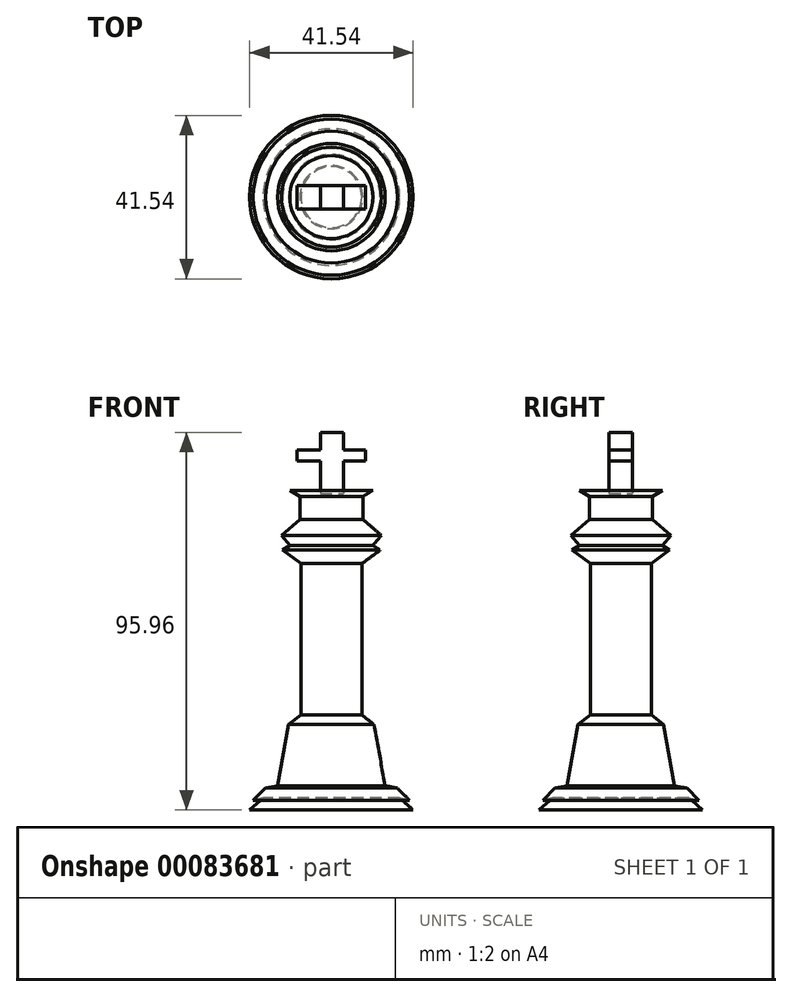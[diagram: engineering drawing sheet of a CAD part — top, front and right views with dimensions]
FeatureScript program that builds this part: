
annotation { "Feature Type Name" : "Feature", "Feature Type Description" : "" }
export const myFeature = defineFeature(function(context is Context, id is Id, definition is map)
    precondition{}
    {
        {
            var Q0;
            Q0=qCreatedBy(makeId("Front.planeOp"),FACE);
            var sketch = newSketch(context, id + "F0", { "sketchPlane" : qUnion([Q0])});
            skLineSegment(sketch, "E0", {"start": v(0, -44.96) * mm, "end": v(20.77, -44.96) * mm});
            skLineSegment(sketch, "E1", {"start": v(20.77, -44.96) * mm, "end": v(17.36, -41.86) * mm});
            skLineSegment(sketch, "E2", {"start": v(17.36, -41.86) * mm, "end": v(19.84, -42.48) * mm});
            skLineSegment(sketch, "E3", {"start": v(19.84, -42.48) * mm, "end": v(16.74, -39.38) * mm});
            skLineSegment(sketch, "E4", {"start": v(16.74, -39.38) * mm, "end": v(13.64, -38.75) * mm});
            skLineSegment(sketch, "E5", {"start": v(13.64, -38.75) * mm, "end": v(10.85, -23.25) * mm});
            skLineSegment(sketch, "E6", {"start": v(10.85, -23.25) * mm, "end": v(7.75, -20.77) * mm});
            skLineSegment(sketch, "E7", {"start": v(7.75, -20.77) * mm, "end": v(7.75, 17.67) * mm});
            skLineSegment(sketch, "E8", {"start": v(7.75, 17.67) * mm, "end": v(12.4, 21.08) * mm});
            skLineSegment(sketch, "E9", {"start": v(12.4, 21.08) * mm, "end": v(10.54, 22.32) * mm});
            skLineSegment(sketch, "E10", {"start": v(10.54, 22.32) * mm, "end": v(12.71, 24.8) * mm});
            skLineSegment(sketch, "E11", {"start": v(12.71, 24.8) * mm, "end": v(8.01, 28.91) * mm});
            skLineSegment(sketch, "E12", {"start": v(8.01, 28.91) * mm, "end": v(8.01, 34.72) * mm});
            skLineSegment(sketch, "E13", {"start": v(8.01, 34.72) * mm, "end": v(10.54, 36.27) * mm});
            skLineSegment(sketch, "E14", {"start": v(10.54, 36.27) * mm, "end": v(0, 36.27) * mm});
            skLineSegment(sketch, "E15", {"start": v(0, 36.27) * mm, "end": v(0, -44.96) * mm});
            skSolve(sketch);
        }
        {
            var Q0;
            Q0=makeQuery(id+"F0.imprint","IMPRINT",FACE,{"disambiguationData":[TD([[makeQuery(id+"F0.imprint","IMPRINT",EDGE,{"derivedFrom":sQuery(id+"F0.wireOp",EDGE,"E0")}),1.0]])]});
            var Q1;
            Q1=sQuery(id+"F0.wireOp",EDGE,"E15");
            revolve(context, id + "F1", {"entities" : qUnion([Q0]), "axis" : qUnion([Q1]), "revolveType" : RevolveType.FULL});
        }
        {
            var Q0;
            Q0=qCreatedBy(makeId("Front.planeOp"),FACE);
            var sketch = newSketch(context, id + "F2", { "sketchPlane" : qUnion([Q0])});
            skLineSegment(sketch, "E16.bottom", {"start": v(-2.8, 51) * mm, "end": v(3.1, 51) * mm});
            skLineSegment(sketch, "E16.top", {"start": v(-2.8, 35.49) * mm, "end": v(3.1, 35.49) * mm});
            skLineSegment(sketch, "E16.left", {"start": v(-2.8, 51) * mm, "end": v(-2.8, 35.49) * mm});
            skLineSegment(sketch, "E16.right", {"start": v(3.1, 51) * mm, "end": v(3.1, 35.49) * mm});
            skLineSegment(sketch, "E17.bottom", {"start": v(-8.68, 46.5) * mm, "end": v(8.68, 46.5) * mm});
            skLineSegment(sketch, "E17.top", {"start": v(-8.68, 43.72) * mm, "end": v(8.68, 43.72) * mm});
            skLineSegment(sketch, "E17.left", {"start": v(-8.68, 46.5) * mm, "end": v(-8.68, 43.72) * mm});
            skLineSegment(sketch, "E17.right", {"start": v(8.68, 46.5) * mm, "end": v(8.68, 43.72) * mm});
            skSolve(sketch);
        }
        {
            var Q0;
            {var subQ0=sQuery(id+"F2.wireOp",EDGE,"E16.top");Q0=makeQuery(id+"F2.imprint","IMPRINT",FACE,{"disambiguationData":[TD([[makeQuery(id+"F2.imprint","IMPRINT",EDGE,{"derivedFrom":subQ0}),1.0]])]});}
            var Q1;
            {var subQ5=sQuery(id+"F2.wireOp",EDGE,"E17.left");Q1=makeQuery(id+"F2.imprint","IMPRINT",FACE,{"disambiguationData":[TD([[makeQuery(id+"F2.imprint","IMPRINT",EDGE,{"derivedFrom":subQ5}),1.0]])]});}
            var Q2;
            {var subQ0=sQuery(id+"F2.wireOp",EDGE,"E17.bottom");var subQ1=sQuery(id+"F2.wireOp",EDGE,"E16.left");var subQ2=makeQuery(id+"F2.imprint","INTERSECT",VERTEX,{"derivedFrom":[subQ1,subQ0]});Q2=makeQuery(id+"F2.imprint","IMPRINT",FACE,{"disambiguationData":[TD([[makeQuery(id+"F2.imprint","IMPRINT",EDGE,{"disambiguationData":[TD([[subQ2,-1.0]])],"derivedFrom":subQ1}),1.0]])]});}
            var Q3;
            {var subQ5=sQuery(id+"F2.wireOp",EDGE,"E17.right");Q3=makeQuery(id+"F2.imprint","IMPRINT",FACE,{"disambiguationData":[TD([[makeQuery(id+"F2.imprint","IMPRINT",EDGE,{"derivedFrom":subQ5}),-1.0]])]});}
            var Q4;
            {var subQ0=sQuery(id+"F2.wireOp",EDGE,"E16.bottom");Q4=makeQuery(id+"F2.imprint","IMPRINT",FACE,{"disambiguationData":[TD([[makeQuery(id+"F2.imprint","IMPRINT",EDGE,{"derivedFrom":subQ0}),-1.0]])]});}
            extrude(context, id + "F3", {"entities" : qUnion([Q0, Q1, Q2, Q3, Q4]), "depth" : 3 * mm, "hasSecondDirection" : true, "secondDirectionOppositeDirection" : true, "secondDirectionDepth" : 3 * mm});
        }
    });
